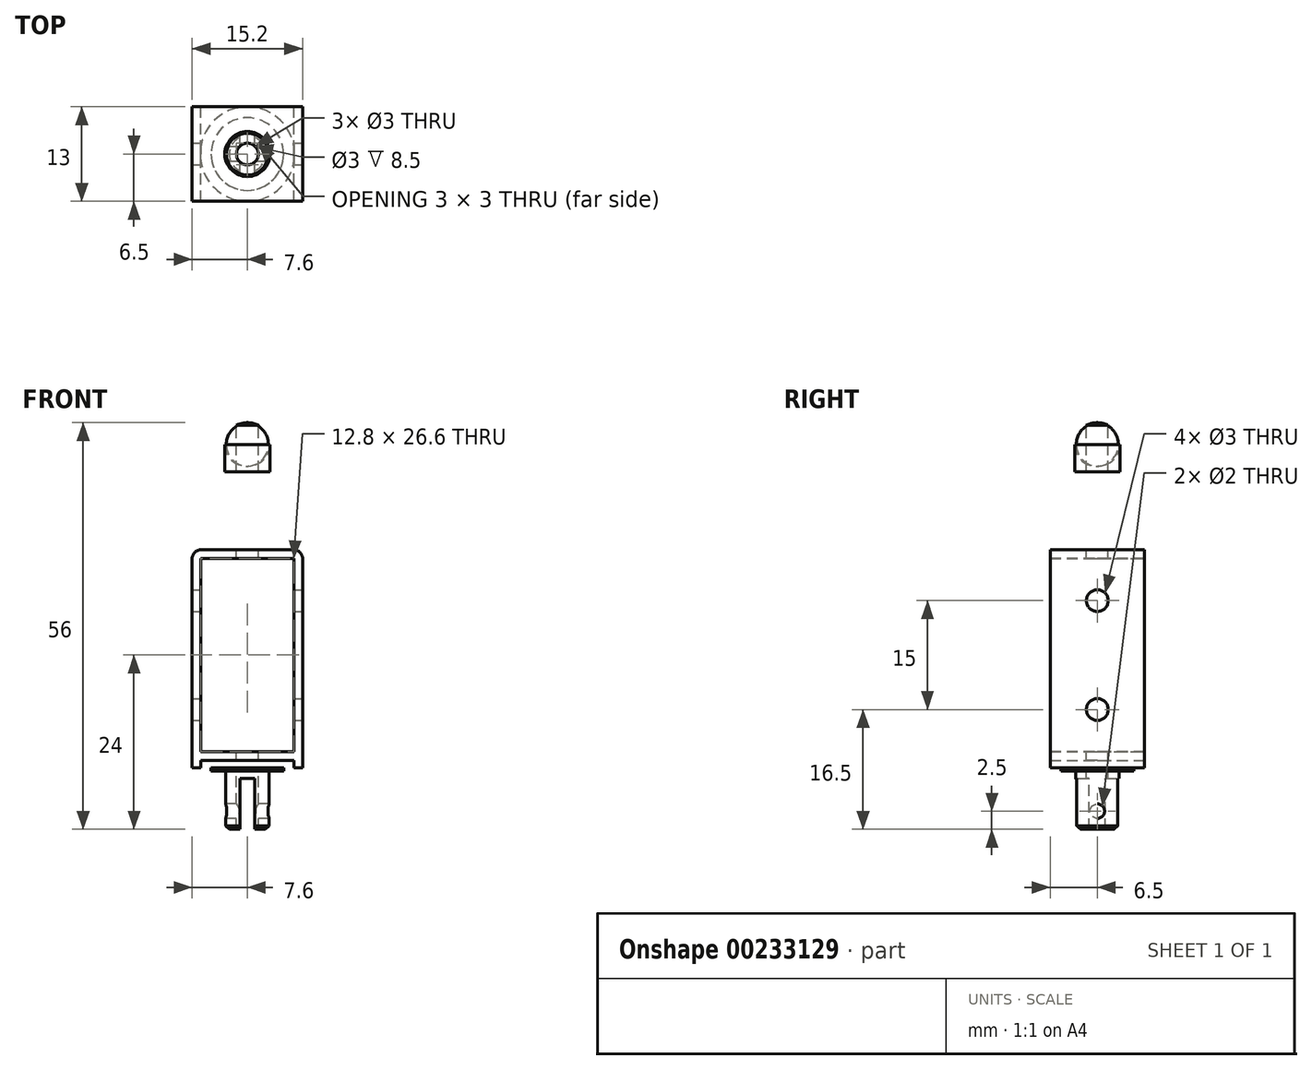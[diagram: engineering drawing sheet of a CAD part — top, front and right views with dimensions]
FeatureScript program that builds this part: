
annotation { "Feature Type Name" : "Feature", "Feature Type Description" : "" }
export const myFeature = defineFeature(function(context is Context, id is Id, definition is map)
    precondition{}
    {
        {
            var Q0;
            Q0=qCreatedBy(makeId("Front.planeOp"),FACE);
            var sketch = newSketch(context, id + "F0", { "sketchPlane" : qUnion([Q0])});
            skLineSegment(sketch, "E0.bottom", {"start": v(7.6, 15) * mm, "end": v(-7.6, 15) * mm});
            skLineSegment(sketch, "E0.top", {"start": v(7.6, -15) * mm, "end": v(-7.6, -15) * mm});
            skLineSegment(sketch, "E0.left", {"start": v(7.6, 15) * mm, "end": v(7.6, -15) * mm});
            skLineSegment(sketch, "E0.right", {"start": v(-7.6, 15) * mm, "end": v(-7.6, -15) * mm});
            skPoint(sketch, "E0.middle", {"position": v(0, 0) * mm});
            skSolve(sketch);
        }
        {
            var Q0;
            Q0 = qSketchRegion(id + "F0", true);
            extrude(context, id + "F1", {"entities" : qUnion([Q0]), "depth" : 13 * mm, "symmetric" : true});
        }
        {
            var Q0;
            Q0=qCreatedBy(makeId("Right.planeOp"),FACE);
            var sketch = newSketch(context, id + "F2", { "sketchPlane" : qUnion([Q0])});
            skLineSegment(sketch, "E1", {"start": v(0, 32.5) * mm, "end": v(0, -23.5) * mm});
            skLineSegment(sketch, "E2", {"start": v(0, -23.5) * mm, "end": v(-3, -23.5) * mm});
            skLineSegment(sketch, "E3", {"start": v(-3, -23.5) * mm, "end": v(-3, -15.5) * mm});
            skLineSegment(sketch, "E4", {"start": v(-3, -15.5) * mm, "end": v(-5, -15.5) * mm});
            skLineSegment(sketch, "E5", {"start": v(-5, -15.5) * mm, "end": v(-5, -14.8) * mm});
            skLineSegment(sketch, "E6", {"start": v(-5, -14.8) * mm, "end": v(-1.5, -14.8) * mm});
            skLineSegment(sketch, "E7", {"start": v(-1.5, -14.8) * mm, "end": v(-1.5, 25.75) * mm});
            skLineSegment(sketch, "E8", {"start": v(-1.5, 25.75) * mm, "end": v(-3.1, 25.75) * mm});
            skLineSegment(sketch, "E9", {"start": v(-3.1, 25.75) * mm, "end": v(-3.1, 32.5) * mm});
            skLineSegment(sketch, "E10", {"start": v(-3.1, 32.5) * mm, "end": v(0, 32.5) * mm});
            skSolve(sketch);
        }
        {
            var Q0;
            Q0 = qSketchRegion(id + "F2", true);
            var Q1;
            Q1=sQuery(id+"F2.wireOp",EDGE,"E1");
            revolve(context, id + "F3", {"entities" : qUnion([Q0]), "axis" : qUnion([Q1]), "revolveType" : RevolveType.FULL});
        }
        {
            var Q0;
            Q0=makeQuery(id+"F3.opRevolve","SWEPT_EDGE",EDGE,{"disambiguationData":[OSD([sQuery(id+"F2.wireOp",EDGE,"E9"),sQuery(id+"F2.wireOp",EDGE,"E10")])]});
            fillet(context, id + "F4", {"entities" : qUnion([Q0]), "radius" : 3 * mm, "tangentPropagation" : true, "allowEdgeOverflow" : false});
        }
        {
            var Q0;
            Q0=qCreatedBy(makeId("Right.planeOp"),FACE);
            var sketch = newSketch(context, id + "F5", { "sketchPlane" : qUnion([Q0])});
            skLineSegment(sketch, "E11", {"start": v(0, 8) * mm, "end": v(0, -7) * mm, "construction": true});
            skCircle(sketch, "E12", {"center": v(0, 8) * mm, "radius": 1.5 * mm});
            skCircle(sketch, "E13", {"center": v(0, -7) * mm, "radius": 1.5 * mm});
            skLineSegment(sketch, "E14", {"start": v(0, -7) * mm, "end": v(0, -21) * mm, "construction": true});
            skCircle(sketch, "E15", {"center": v(0, -21) * mm, "radius": 1 * mm});
            skSolve(sketch);
        }
        {
            var Q0;
            Q0=makeQuery(id+"F5.imprint","IMPRINT",FACE,{"disambiguationData":[TD([[makeQuery(id+"F5.imprint","IMPRINT",EDGE,{"derivedFrom":sQuery(id+"F5.wireOp",EDGE,"E13")}),1.0]])]});
            var Q1;
            Q1=makeQuery(id+"F5.imprint","IMPRINT",FACE,{"disambiguationData":[TD([[makeQuery(id+"F5.imprint","IMPRINT",EDGE,{"derivedFrom":sQuery(id+"F5.wireOp",EDGE,"E12")}),1.0]])]});
            extrude(context, id + "F6", {"entities" : qUnion([Q0, Q1]), "operationType" : NewBodyOperationType.REMOVE, "endBound" : BoundingType.THROUGH_ALL, "oppositeDirection" : true, "depth" : 25 * mm, "hasSecondDirection" : true, "secondDirectionBound" : BoundingType.THROUGH_ALL, "secondDirectionOppositeDirection" : false, "secondDirectionDepth" : 25 * mm});
        }
        {
            var Q0;
            Q0=makeQuery(id+"F5.imprint","IMPRINT",FACE,{"disambiguationData":[TD([[makeQuery(id+"F5.imprint","IMPRINT",EDGE,{"derivedFrom":sQuery(id+"F5.wireOp",EDGE,"E15")}),1.0]])]});
            extrude(context, id + "F7", {"entities" : qUnion([Q0]), "operationType" : NewBodyOperationType.REMOVE, "endBound" : BoundingType.THROUGH_ALL, "depth" : 25 * mm, "hasSecondDirection" : true, "secondDirectionBound" : BoundingType.THROUGH_ALL, "secondDirectionOppositeDirection" : true, "secondDirectionDepth" : 25 * mm});
        }
        {
            var Q0;
            Q0=qCreatedBy(makeId("Front.planeOp"),FACE);
            var sketch = newSketch(context, id + "F8", { "sketchPlane" : qUnion([Q0])});
            skLineSegment(sketch, "E16.bottom", {"start": v(1, -23.5) * mm, "end": v(-1, -23.5) * mm});
            skLineSegment(sketch, "E16.top", {"start": v(1, -16.5) * mm, "end": v(-1, -16.5) * mm});
            skLineSegment(sketch, "E16.left", {"start": v(1, -23.5) * mm, "end": v(1, -16.5) * mm});
            skLineSegment(sketch, "E16.right", {"start": v(-1, -23.5) * mm, "end": v(-1, -16.5) * mm});
            skPoint(sketch, "E16.middle", {"position": v(0, -20) * mm});
            skSolve(sketch);
        }
        {
            var Q0;
            Q0=makeQuery(id+"F3.opRevolve","SWEPT_EDGE",EDGE,{"disambiguationData":[OSD([sQuery(id+"F2.wireOp",EDGE,"E2"),sQuery(id+"F2.wireOp",EDGE,"E3")])]});
            chamfer(context, id + "F9", {"entities" : qUnion([Q0]), "width" : .5 * mm, "tangentPropagation" : true});
        }
        {
            var Q0;
            Q0 = qSketchRegion(id + "F8", true);
            extrude(context, id + "F10", {"entities" : qUnion([Q0]), "operationType" : NewBodyOperationType.REMOVE, "endBound" : BoundingType.THROUGH_ALL, "depth" : 25 * mm, "hasSecondDirection" : true, "secondDirectionBound" : BoundingType.THROUGH_ALL, "secondDirectionOppositeDirection" : true, "secondDirectionDepth" : 25 * mm});
        }
        {
            var Q0;
            Q0=qCreatedBy(makeId("Top.planeOp"),FACE);
            var sketch = newSketch(context, id + "F11", { "sketchPlane" : qUnion([Q0])});
            skCircle(sketch, "E17.0", {"center": v(0, 0) * mm, "radius": 1.5 * mm});
            skSolve(sketch);
        }
        {
            var Q0;
            Q0 = qSketchRegion(id + "F11", true);
            extrude(context, id + "F12", {"entities" : qUnion([Q0]), "operationType" : NewBodyOperationType.REMOVE, "endBound" : BoundingType.THROUGH_ALL, "oppositeDirection" : true, "depth" : 25 * mm, "hasSecondDirection" : true, "secondDirectionBound" : BoundingType.THROUGH_ALL, "secondDirectionOppositeDirection" : false, "secondDirectionDepth" : 25 * mm});
        }
        {
            var Q0;
            Q0=makeQuery(id+"F1.opExtrude","SWEPT_EDGE",EDGE,{"disambiguationData":[OSD([sQuery(id+"F0.wireOp",EDGE,"E0.bottom"),sQuery(id+"F0.wireOp",EDGE,"E0.left")])]});
            var Q1;
            Q1=makeQuery(id+"F1.opExtrude","SWEPT_EDGE",EDGE,{"disambiguationData":[OSD([sQuery(id+"F0.wireOp",EDGE,"E0.bottom"),sQuery(id+"F0.wireOp",EDGE,"E0.right")])]});
            fillet(context, id + "F13", {"entities" : qUnion([Q0, Q1]), "radius" : 1.2 * mm, "tangentPropagation" : true, "allowEdgeOverflow" : false});
        }
        {
            var Q0;
            Q0=makeQuery(id+"F1.opExtrude","CAP_FACE",FACE,{"disambiguationData":[OSD([sQuery(id+"F0.wireOp",EDGE,"E0.bottom"),sQuery(id+"F0.wireOp",EDGE,"E0.top"),sQuery(id+"F0.wireOp",EDGE,"E0.left"),sQuery(id+"F0.wireOp",EDGE,"E0.right")])],"isStart":true});
            var sketch = newSketch(context, id + "F14", { "sketchPlane" : qUnion([Q0])});
            skLineSegment(sketch, "E18.bottom", {"start": v(6.4, 13.8) * mm, "end": v(-6.4, 13.8) * mm});
            skLineSegment(sketch, "E18.top", {"start": v(6.4, -12.8) * mm, "end": v(-6.4, -12.8) * mm});
            skLineSegment(sketch, "E18.left", {"start": v(6.4, 13.8) * mm, "end": v(6.4, -12.8) * mm});
            skLineSegment(sketch, "E18.right", {"start": v(-6.4, 13.8) * mm, "end": v(-6.4, -12.8) * mm});
            skPoint(sketch, "E18.middle", {"position": v(0, 0.5) * mm});
            skLineSegment(sketch, "E19.bottom", {"start": v(-6.4, -15) * mm, "end": v(6.4, -15) * mm});
            skLineSegment(sketch, "E19.top", {"start": v(-6.4, -14) * mm, "end": v(6.4, -14) * mm});
            skLineSegment(sketch, "E19.left", {"start": v(-6.4, -15) * mm, "end": v(-6.4, -14) * mm});
            skLineSegment(sketch, "E19.right", {"start": v(6.4, -15) * mm, "end": v(6.4, -14) * mm});
            skLineSegment(sketch, "E20", {"start": v(-6.4, -12.8) * mm, "end": v(-6.4, -14) * mm, "construction": true});
            skLineSegment(sketch, "E21", {"start": v(-6.4, -15) * mm, "end": v(-7.6, -15) * mm, "construction": true});
            skSolve(sketch);
        }
        {
            var Q0;
            Q0 = qSketchRegion(id + "F14", true);
            extrude(context, id + "F15", {"entities" : qUnion([Q0]), "operationType" : NewBodyOperationType.REMOVE, "endBound" : BoundingType.THROUGH_ALL, "oppositeDirection" : true, "depth" : 25 * mm, "hasSecondDirection" : true, "secondDirectionBound" : BoundingType.THROUGH_ALL, "secondDirectionOppositeDirection" : false, "secondDirectionDepth" : 25 * mm});
        }
        {
            var Q0;
            Q0=qCreatedBy(makeId("Top.planeOp"),FACE);
            var sketch = newSketch(context, id + "F16", { "sketchPlane" : qUnion([Q0])});
            skCircle(sketch, "E22", {"center": v(0, 0) * mm, "radius": 6.5 * mm});
            skSolve(sketch);
        }
        {
            var Q0;
            Q0 = qSketchRegion(id + "F16", true);
            var Q1;
            Q1=makeQuery(id+"F15.boolean.opBoolean","COPY",FACE,{"derivedFrom":makeQuery(id+"F15.opExtrude","SWEPT_FACE",FACE,{"disambiguationData":[OSD([sQuery(id+"F14.wireOp",EDGE,"E18.bottom")])]})});
            var Q2;
            Q2=makeQuery(id+"F15.boolean.opBoolean","COPY",FACE,{"derivedFrom":makeQuery(id+"F15.opExtrude","SWEPT_FACE",FACE,{"disambiguationData":[OSD([sQuery(id+"F14.wireOp",EDGE,"E18.top")])]})});
            extrude(context, id + "F17", {"entities" : qUnion([Q0]), "endBound" : BoundingType.UP_TO_SURFACE, "endBoundEntityFace" : qUnion([Q1]), "depth" : 25 * mm, "hasSecondDirection" : true, "secondDirectionBound" : BoundingType.UP_TO_SURFACE, "secondDirectionOppositeDirection" : true, "secondDirectionBoundEntityFace" : qUnion([Q2]), "secondDirectionDepth" : 25 * mm});
        }
    });
